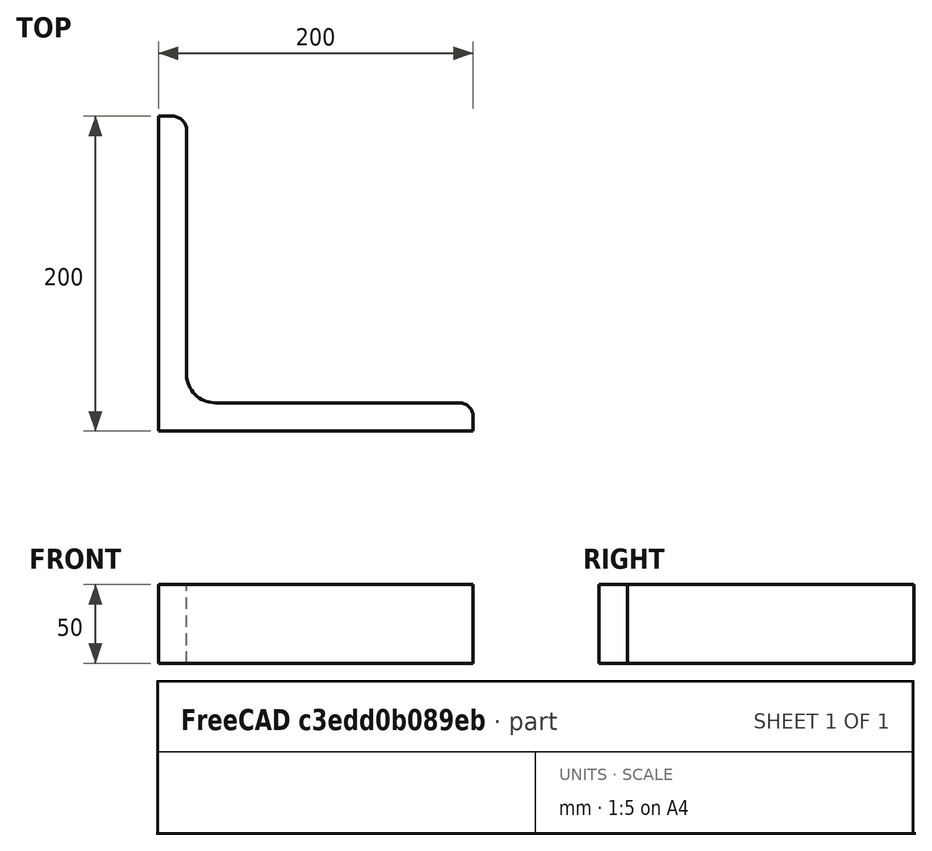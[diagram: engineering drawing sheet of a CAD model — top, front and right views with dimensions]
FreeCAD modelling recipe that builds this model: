
FCSTD DOCUMENT  (FreeCAD 0.15R4671 (Git))
Label: Angle Bar L200x200x18 EN10056 S235JR
License: All rights reserved
LicenseURL: http://en.wikipedia.org/wiki/All_rights_reserved
objects: Sketcher::SketchObject×1, Part::Extrusion×1
note: 2 computed .brp shape members not serialized (recipe doc carries the construction recipe); baked Part::Feature solids carry a one-line shape summary decoded from their .brp

FEATURE [Sketcher::SketchObject] Sketch
  sketch-geometry (9):
    g0: LineSegment StartX=0 StartY=0 StartZ=0 EndX=200 EndY=0 EndZ=0
    g1: LineSegment StartX=200 StartY=0 StartZ=0 EndX=200 EndY=9 EndZ=0
    g2: LineSegment StartX=191 StartY=18 StartZ=0 EndX=36 EndY=18 EndZ=0
    g3: LineSegment StartX=0 StartY=0 StartZ=0 EndX=0 EndY=200 EndZ=0
    g4: LineSegment StartX=0 StartY=200 StartZ=0 EndX=9 EndY=200 EndZ=0
    g5: LineSegment StartX=18 StartY=191 StartZ=0 EndX=18 EndY=36 EndZ=0
    g6: ArcOfCircle CenterX=36 CenterY=36 CenterZ=0 NormalX=0 NormalY=0 NormalZ=1 Radius=18 StartAngle=3.14159 EndAngle=4.71239
    g7: ArcOfCircle CenterX=9 CenterY=191 CenterZ=0 NormalX=0 NormalY=0 NormalZ=1 Radius=9 StartAngle=0 EndAngle=1.5708
    g8: ArcOfCircle CenterX=191 CenterY=9 CenterZ=0 NormalX=0 NormalY=0 NormalZ=1 Radius=9 StartAngle=0 EndAngle=1.5708
  constraints (23):
    c: Coincident(g0,g-1)
    c: Horizontal(g0)
    c: Coincident(g1,g0)
    c: Vertical(g1)
    c: Horizontal(g2)
    c: Coincident(g3,g-1)
    c: Vertical(g3)
    c: Coincident(g4,g3)
    c: Horizontal(g4)
    c: Vertical(g5)
    c: Tangent(g5,g6) = -1.5708
    c: Tangent(g2,g6) = 1.5708
    c: Tangent(g4,g7) = 1.5708
    c: Tangent(g5,g7) = 1.5708
    c: Tangent(g2,g8) = -1.5708
    c: Tangent(g1,g8) = -1.5708
    c: DistanceX(g0) = 200
    c: DistanceY(g3) = 200
    c: DistanceY(g0,g2) = 18
    c: DistanceX(g3,g5) = 18
    c: Radius(g6) = 18
    c: Radius(g8) = 9
    c: Radius(g7) = 9
FEATURE [Part::Extrusion] Extrude  label="Angle Bar L200x200x18 EN10056 S235JR"
  Base = -> Sketch
  Dir = (0,0,50)
  Solid = true
